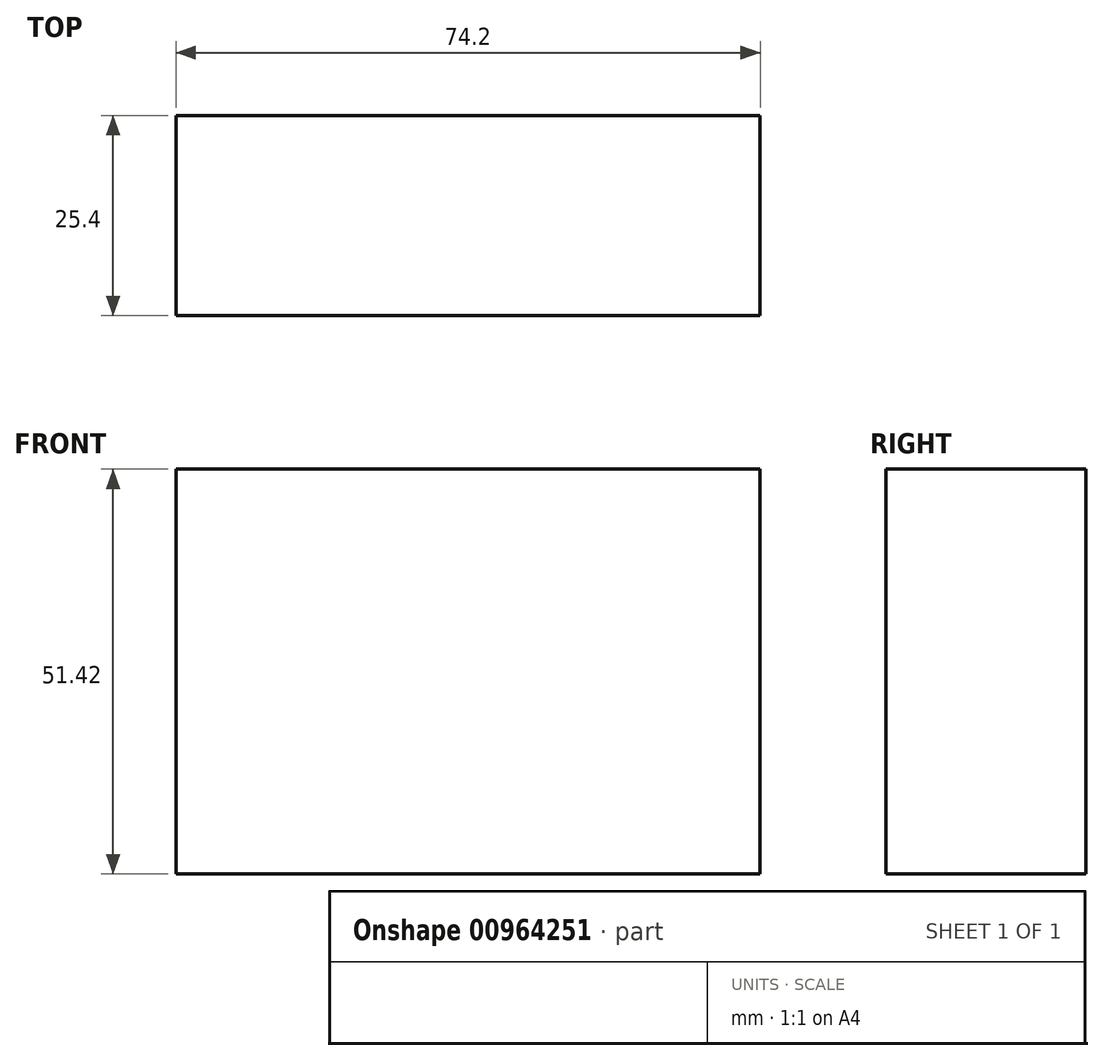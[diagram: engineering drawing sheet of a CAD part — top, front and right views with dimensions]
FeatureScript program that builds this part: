
annotation { "Feature Type Name" : "Feature", "Feature Type Description" : "" }
export const myFeature = defineFeature(function(context is Context, id is Id, definition is map)
    precondition{}
    {
        {
            var Q0;
            Q0=qCreatedBy(makeId("Front.planeOp"),FACE);
            var sketch = newSketch(context, id + "F0", { "sketchPlane" : qUnion([Q0])});
            skLineSegment(sketch, "E0.bottom", {"start": v(37.1, 25.71) * mm, "end": v(-37.1, 25.71) * mm});
            skLineSegment(sketch, "E0.top", {"start": v(37.1, -25.71) * mm, "end": v(-37.1, -25.71) * mm});
            skLineSegment(sketch, "E0.left", {"start": v(37.1, 25.71) * mm, "end": v(37.1, -25.71) * mm});
            skLineSegment(sketch, "E0.right", {"start": v(-37.1, 25.71) * mm, "end": v(-37.1, -25.71) * mm});
            skPoint(sketch, "E0.middle", {"position": v(0, 0) * mm});
            skSolve(sketch);
        }
        {
            var Q0;
            Q0 = qSketchRegion(id + "F0", true);
            extrude(context, id + "F1", {"entities" : qUnion([Q0]), "depth" : 25.4 * mm, "offsetDistance" : 25.4 * mm});
        }
    });
